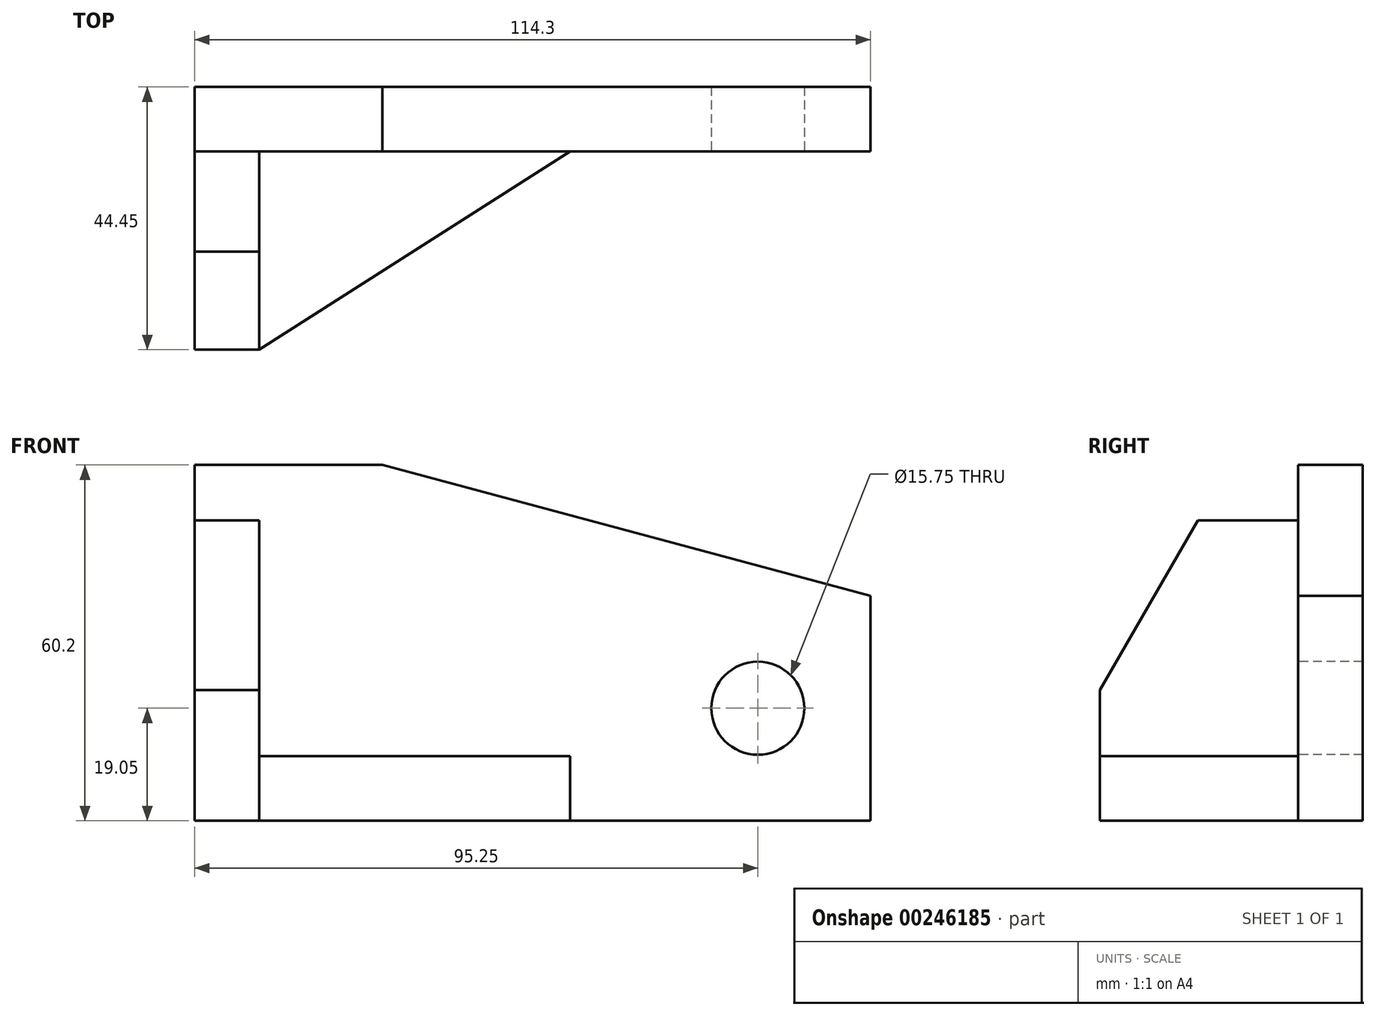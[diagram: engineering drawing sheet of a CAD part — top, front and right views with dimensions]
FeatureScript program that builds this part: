
annotation { "Feature Type Name" : "Feature", "Feature Type Description" : "" }
export const myFeature = defineFeature(function(context is Context, id is Id, definition is map)
    precondition{}
    {
        {
            var Q0;
            Q0=qCreatedBy(makeId("Front.planeOp"),FACE);
            var sketch = newSketch(context, id + "F0", { "sketchPlane" : qUnion([Q0])});
            skLineSegment(sketch, "E0.bottom", {"start": v(0, 60.2) * mm, "end": v(31.75, 60.2) * mm});
            skLineSegment(sketch, "E0.top", {"start": v(0, 0) * mm, "end": v(114.3, 0) * mm});
            skLineSegment(sketch, "E0.left", {"start": v(0, 60.2) * mm, "end": v(0, 0) * mm});
            skLineSegment(sketch, "E0.right", {"start": v(114.3, 38.08) * mm, "end": v(114.3, 0) * mm});
            skLineSegment(sketch, "E1", {"start": v(31.75, 60.2) * mm, "end": v(114.3, 38.08) * mm});
            skSolve(sketch);
        }
        {
            var Q0;
            Q0 = qSketchRegion(id + "F0", true);
            extrude(context, id + "F1", {"entities" : qUnion([Q0]), "oppositeDirection" : true, "depth" : 10.92 * mm});
        }
        {
            var Q0;
            Q0=qCreatedBy(makeId("Top.planeOp"),FACE);
            var sketch = newSketch(context, id + "F2", { "sketchPlane" : qUnion([Q0])});
            skLineSegment(sketch, "E2.right", {"start": v(10.92, 0) * mm, "end": v(10.92, -33.53) * mm});
            skLineSegment(sketch, "E3", {"start": v(10.92, -33.53) * mm, "end": v(63.5, 0) * mm});
            skLineSegment(sketch, "E4", {"start": v(10.92, 0) * mm, "end": v(63.5, 0) * mm});
            skSolve(sketch);
        }
        {
            var Q0;
            Q0=qCreatedBy(makeId("Right.planeOp"),FACE);
            var sketch = newSketch(context, id + "F3", { "sketchPlane" : qUnion([Q0])});
            skLineSegment(sketch, "E5.bottom", {"start": v(0, 0) * mm, "end": v(-33.53, 0) * mm});
            skLineSegment(sketch, "E5.top", {"start": v(0, 50.8) * mm, "end": v(-16.96, 50.8) * mm});
            skLineSegment(sketch, "E5.left", {"start": v(0, 0) * mm, "end": v(0, 50.8) * mm});
            skLineSegment(sketch, "E5.right", {"start": v(-33.53, 0) * mm, "end": v(-33.53, 22.1) * mm});
            skLineSegment(sketch, "E6", {"start": v(-33.53, 22.1) * mm, "end": v(-16.96, 50.8) * mm});
            skSolve(sketch);
        }
        {
            var Q0;
            Q0 = qSketchRegion(id + "F3", true);
            extrude(context, id + "F4", {"entities" : qUnion([Q0]), "operationType" : NewBodyOperationType.ADD, "depth" : 10.92 * mm});
        }
        {
            var Q0;
            Q0 = qSketchRegion(id + "F2", true);
            extrude(context, id + "F5", {"entities" : qUnion([Q0]), "operationType" : NewBodyOperationType.ADD, "depth" : 10.92 * mm});
        }
        {
            var Q0;
            Q0=makeQuery(id+"F1.opExtrude","CAP_FACE",FACE,{"disambiguationData":[OSD([sQuery(id+"F0.wireOp",EDGE,"E0.bottom"),sQuery(id+"F0.wireOp",EDGE,"E0.top"),sQuery(id+"F0.wireOp",EDGE,"E0.left"),sQuery(id+"F0.wireOp",EDGE,"E0.right"),sQuery(id+"F0.wireOp",EDGE,"E1")])],"isStart":true});
            var sketch = newSketch(context, id + "F6", { "sketchPlane" : qUnion([Q0])});
            skCircle(sketch, "E7", {"center": v(95.25, 19.05) * mm, "radius": 7.87 * mm});
            skSolve(sketch);
        }
        {
            var Q0;
            Q0=makeQuery(id+"F6.imprint","IMPRINT",FACE,{"disambiguationData":[TD([[makeQuery(id+"F6.imprint","IMPRINT",EDGE,{"derivedFrom":sQuery(id+"F6.wireOp",EDGE,"E7")}),1.0]])]});
            extrude(context, id + "F7", {"entities" : qUnion([Q0]), "operationType" : NewBodyOperationType.REMOVE, "oppositeDirection" : true, "depth" : 10.92 * mm});
        }
    });
